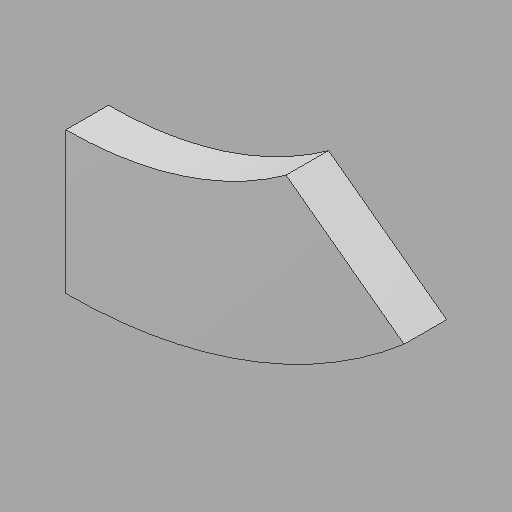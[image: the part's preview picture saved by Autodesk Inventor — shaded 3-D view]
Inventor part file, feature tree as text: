
AUTODESK INVENTOR PART (.ipt)
format: ipt  version: 2022.1 (Build 261234020, 234B)  size: 88,576 bytes
history: imported  units: in
note: dims shown in document units (in); Inventor stores cm internally (conversion verified against a paired STEP export)
features: imported_body x1
ambient origin geometry x8: Origin, YZ Plane, XZ Plane, XY Plane, X Axis, Y Axis, Z Axis, Center Point
bodies: Solid1 (imported_parasolid), Body1 (imported_parasolid)
feature tree (1):
  imported_body  NMx_Import_Brep_tag  [imported B-rep: ~6 faces, bbox_mm=[1213.186396, 761.386567, 152.4]]
